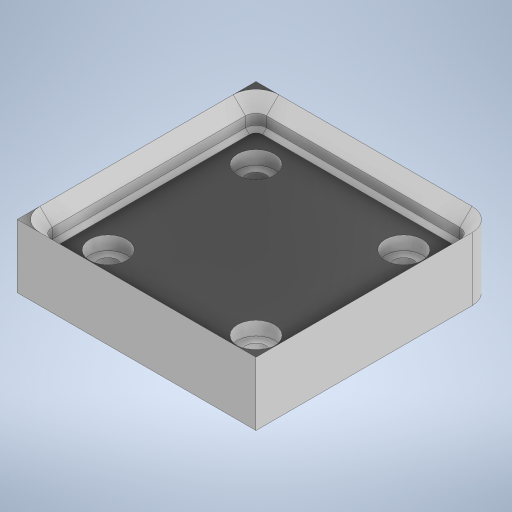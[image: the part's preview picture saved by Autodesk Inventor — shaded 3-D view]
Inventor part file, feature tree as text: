
AUTODESK INVENTOR PART (.ipt)
format: ipt  version: 2023 (Build 270158030, 158C)  size: 357,888 bytes
history: native  units: mm
features: extrude x6, sketch x6, chamfer x2, projected_geometry x1
ambient origin geometry x8: Origin, YZ Plane, XZ Plane, XY Plane, X Axis, Y Axis, Z Axis, Center Point
bodies: Solid1 (feature_tree)
feature tree (15):
  extrude  "square-base"  Depth=42.0mm
  extrude  "Extrusion2"  Depth=4.65mm
  extrude  "Extrusion3"  Depth=2.85mm
  chamfer  "Chamfer2"  [1 undecoded]
  chamfer  "Chamfer1"  Distance=2.15mm
  extrude  "weighted-base"  Depth=2.15mm
  extrude  "Extrusion5"  Depth=2.4mm TaperAngle=0.0deg
  extrude  "Extrusion6"  Depth=2.15mm TaperAngle=45.0deg
  sketch  "Sketch1"  dims[d0=42.0mm d1=42.0mm]
  sketch  "Sketch2"  dims[d2=4.65mm d3=0.0mm d4=2.85mm]
  sketch  "Sketch3"  dims[d5=2.85mm d6=2.85mm]
  sketch  "Sketch5"  dims[d7=2.85mm d8=0.0mm d9=0.0mm]
  projected_geometry  "Projected Loop1"
  sketch  "Sketch6"  dims[d10=2.15mm]
  sketch  "Sketch7"  dims[d12=2.15mm d13=2.15mm d14=2.15mm d15=3.95mm d16=0.0mm d17=2.15mm d18=2.0mm d19=45.0deg d24=0.7mm d25=2.0mm d26=45.0deg d29=1.15mm d30=1.85mm d31=4.0mm d32=6.5mm d33=0.0mm d34=6.5mm d35=8.0mm d36=8.0mm d37=8.0mm d38=8.0mm d39=2.4mm d40=0.0mm d41=3.5mm d42=0.0mm d43=0.0mm d20=0.872665mm d27=0.0mm]
note: 1 required parameter value undecoded (feature->parameter linkage not recoverable at this tier; creation-order binding heuristic only, values carry confidence <= 0.55)
